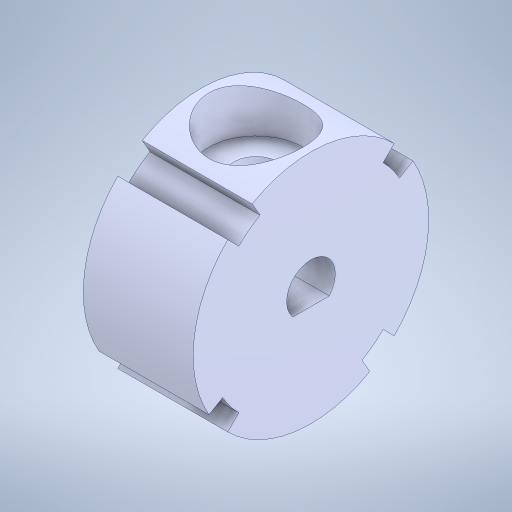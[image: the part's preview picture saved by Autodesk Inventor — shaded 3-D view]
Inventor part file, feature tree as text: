
AUTODESK INVENTOR PART (.ipt)
format: ipt  version: 2023.5 (Build 275446000, 446)  size: 2,463,744 bytes
history: native  units: mm
features: sketch x10, extrude x9, other x4, projected_geometry x4, pattern_circular x1, hole x1, mirror x1, chamfer x1
ambient origin geometry x8: Origin, YZ Plane, XZ Plane, XY Plane, X Axis, Y Axis, Z Axis, Center Point
bodies: Body1 (feature_tree)
feature tree (31):
  extrude  "Wyciągnięcie proste1"  Depth=15.0mm
  extrude  "Wyciągnięcie proste2"  Depth=7.0mm TaperAngle=0.0deg
  sketch  "Szkic3"
  other  "Płaszczyzna konstrukcyjna2"
  extrude  "Wyciągnięcie proste3"  Depth=1.0mm TaperAngle=0.0deg
  pattern_circular  "Szyk kołowy1"  [2 undecoded]
  extrude  "Wyciągnięcie proste4"  TaperAngle=15.0deg  [1 undecoded]
  hole  "Otwór1"  [1 undecoded]
  mirror  "Odbij1"
  extrude  "Wyciągnięcie proste5"  TaperAngle=0.0deg  [1 undecoded]
  extrude  "Wyciągnięcie proste6"  Depth=40.0mm TaperAngle=360.0deg
  sketch  "Szkic11"
  extrude  "Wyciągnięcie proste7"  Depth=3.0mm
  extrude  "Wyciągnięcie proste8"  Depth=10.0mm TaperAngle=0.0deg
  chamfer  "Faza1"  Distance=0.5mm
  extrude  "Wyciągnięcie proste9"  Depth=10.0mm TaperAngle=0.0deg
  other  "Bryła31"
  sketch  "Szkic1"
  sketch  "Szkic2"
  projected_geometry  "Pętla rzutowana1"
  other  "Płaszczyzna konstrukcyjna1"
  sketch  "Szkic5"
  sketch  "Szkic6"
  projected_geometry  "Pętla rzutowana2"
  sketch  "Szkic7"
  sketch  "Szkic8"
  projected_geometry  "Pętla rzutowana3"
  sketch  "Szkic10"
  projected_geometry  "Pętla rzutowana5"
  sketch  "Szkic12"
  other  "Engrane_8:1"
note: 5 required parameter values undecoded (feature->parameter linkage not recoverable at this tier; creation-order binding heuristic only, values carry confidence <= 0.55)
